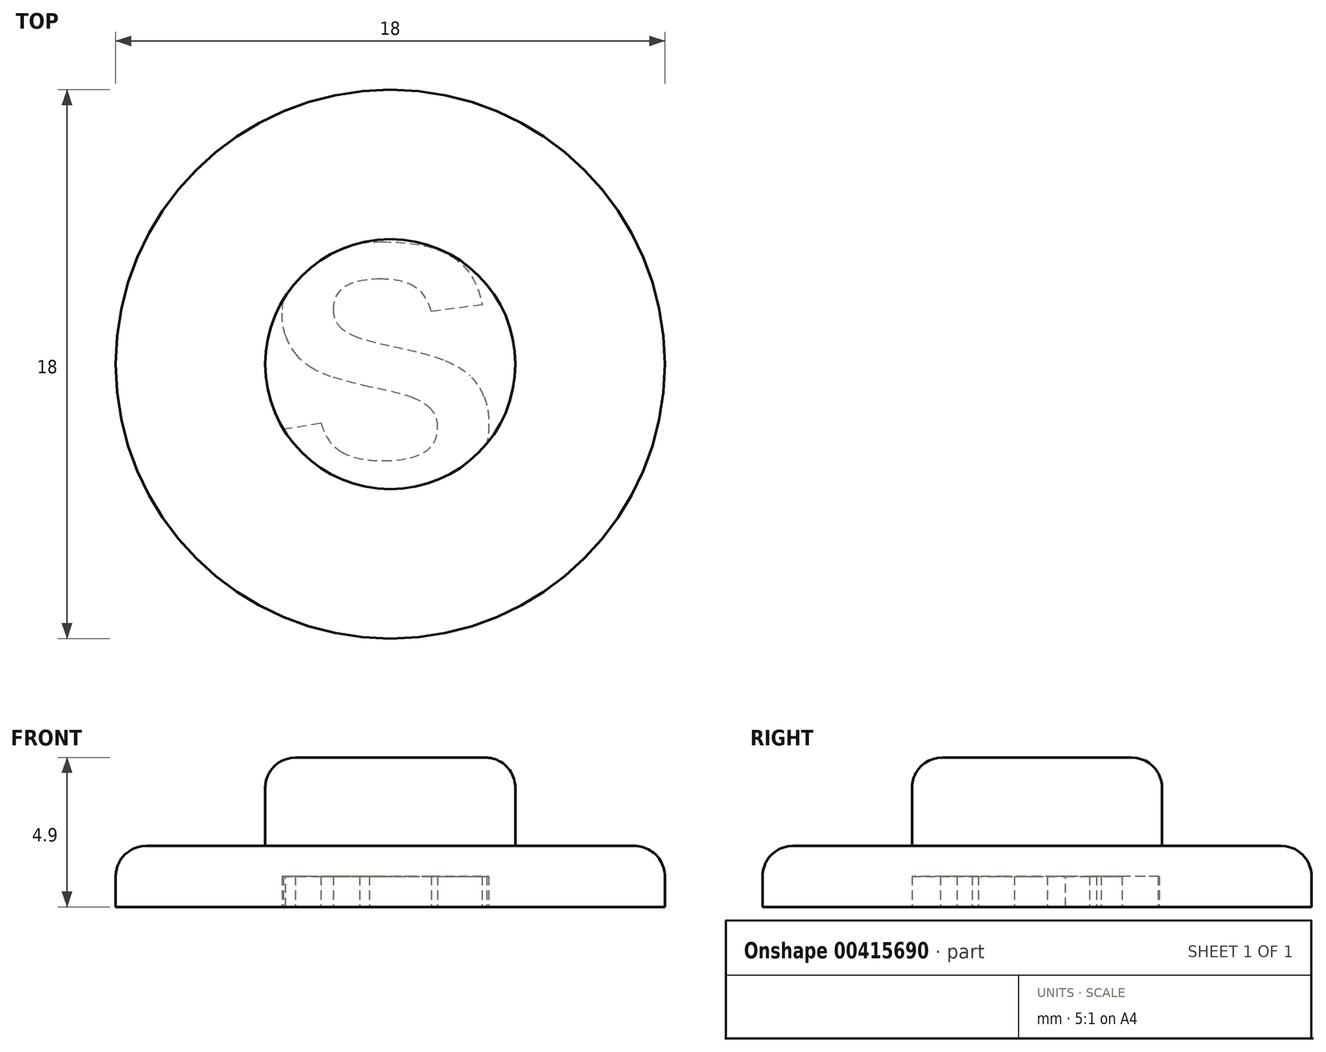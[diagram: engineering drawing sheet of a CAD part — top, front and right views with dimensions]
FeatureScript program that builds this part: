
annotation { "Feature Type Name" : "Feature", "Feature Type Description" : "" }
export const myFeature = defineFeature(function(context is Context, id is Id, definition is map)
    precondition{}
    {
        {
            var Q0;
            Q0=qCreatedBy(makeId("Top.planeOp"),FACE);
            var sketch = newSketch(context, id + "F0", { "sketchPlane" : qUnion([Q0])});
            skCircle(sketch, "E0", {"center": v(0, 0) * mm, "radius": 9 * mm});
            skCircle(sketch, "E1", {"center": v(0, 0) * mm, "radius": 4.1 * mm});
            skSolve(sketch);
        }
        {
            var Q0;
            Q0=makeQuery(id+"F0.imprint","IMPRINT",FACE,{"disambiguationData":[TD([[makeQuery(id+"F0.imprint","IMPRINT",EDGE,{"derivedFrom":sQuery(id+"F0.wireOp",EDGE,"E0")}),1.0]])]});
            var Q1;
            Q1=makeQuery(id+"F0.imprint","IMPRINT",FACE,{"disambiguationData":[TD([[makeQuery(id+"F0.imprint","IMPRINT",EDGE,{"derivedFrom":sQuery(id+"F0.wireOp",EDGE,"E1")}),1.0]])]});
            extrude(context, id + "F1", {"entities" : qUnion([Q0, Q1]), "depth" : 2 * mm});
        }
        {
            var Q0;
            Q0=makeQuery(id+"F0.imprint","IMPRINT",FACE,{"disambiguationData":[TD([[makeQuery(id+"F0.imprint","IMPRINT",EDGE,{"derivedFrom":sQuery(id+"F0.wireOp",EDGE,"E1")}),1.0]])]});
            extrude(context, id + "F2", {"entities" : qUnion([Q0]), "operationType" : NewBodyOperationType.ADD, "depth" : 4.9 * mm});
        }
        {
            var Q0;
            Q0=makeQuery(id+"F0.imprint","IMPRINT",FACE,{"disambiguationData":[TD([[makeQuery(id+"F0.imprint","IMPRINT",EDGE,{"derivedFrom":sQuery(id+"F0.wireOp",EDGE,"E1")}),1.0]])]});
            var sketch = newSketch(context, id + "F3", { "sketchPlane" : qUnion([Q0])});
            skText(sketch, "E2", { "text": "S", "fontName": "Arimo-Bold.ttf"});
            const initialGuessF3  = {"E2": [-0.00428, -0.00434, 1, 0, 0.00861]};
            skSetInitialGuess(sketch, initialGuessF3);
            skSolve(sketch);
        }
        {
            var Q0;
            {var subQ7=sQuery(id+"F3.wireOp",EDGE,"E2.sketch_text.stroke-5");Q0=makeQuery(id+"F3.imprint","IMPRINT",FACE,{"disambiguationData":[TD([[makeQuery(id+"F3.imprint","IMPRINT",EDGE,{"derivedFrom":subQ7}),-1.0]])]});}
            extrude(context, id + "F4", {"entities" : qUnion([Q0]), "operationType" : NewBodyOperationType.REMOVE, "depth" : 1 * mm});
        }
        {
            var Q0;
            Q0=makeQuery(id+"F2.opExtrude","CAP_EDGE",EDGE,{"disambiguationData":[OSD([sQuery(id+"F0.wireOp",EDGE,"E1")])],"isStart":false});
            fillet(context, id + "F5", {"entities" : qUnion([Q0]), "radius" : 1 * mm, "tangentPropagation" : true, "allowEdgeOverflow" : false});
        }
        {
            var Q0;
            Q0=makeQuery(id+"F1.opExtrude","CAP_EDGE",EDGE,{"disambiguationData":[OSD([sQuery(id+"F0.wireOp",EDGE,"E0")])],"isStart":false});
            fillet(context, id + "F6", {"entities" : qUnion([Q0]), "radius" : 1 * mm, "tangentPropagation" : true, "allowEdgeOverflow" : false});
        }
    });
